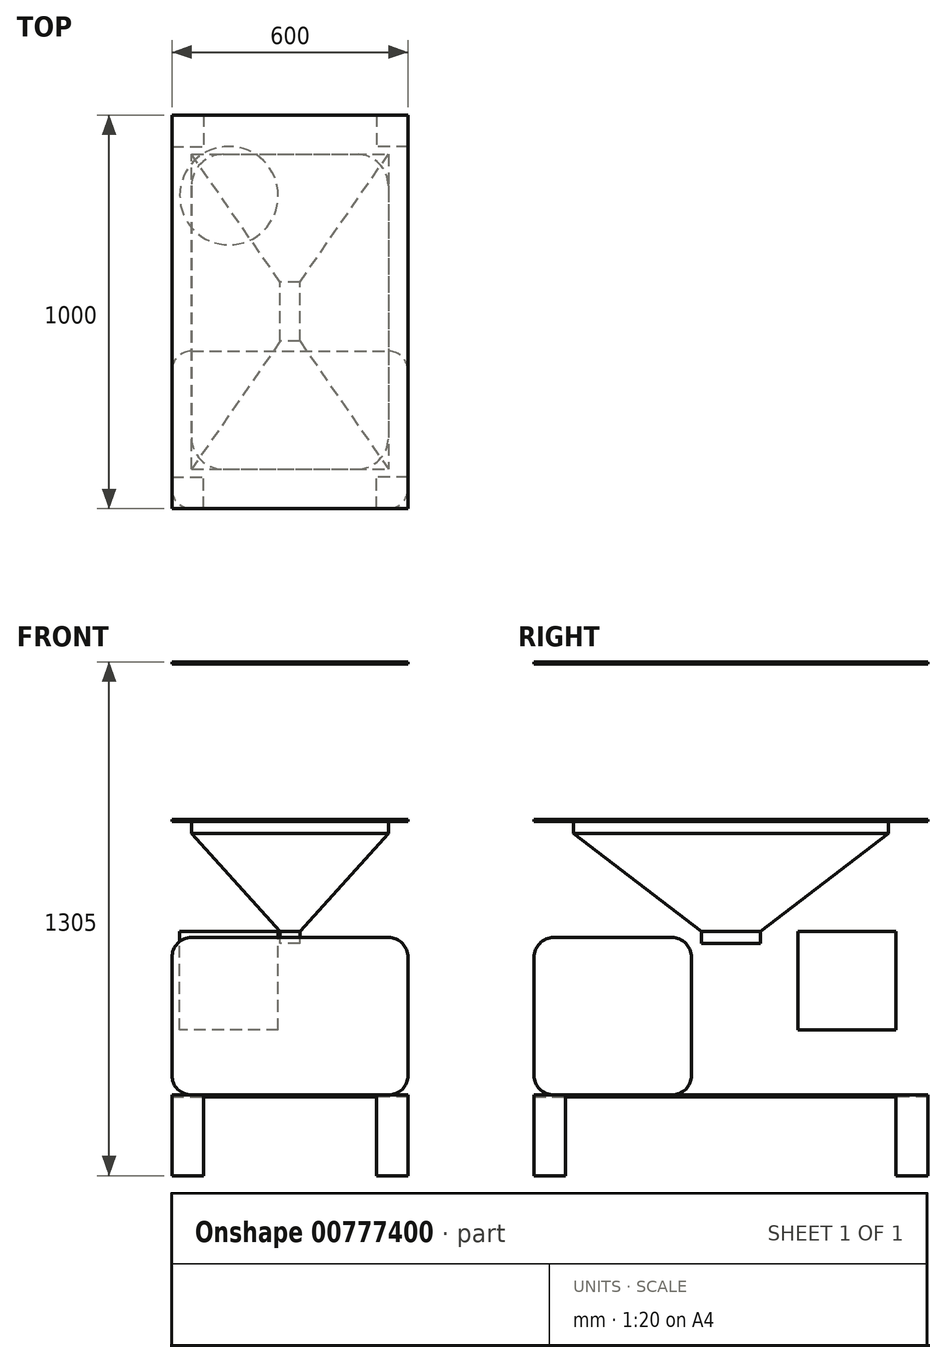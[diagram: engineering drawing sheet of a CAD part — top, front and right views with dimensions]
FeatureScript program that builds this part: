
annotation { "Feature Type Name" : "Feature", "Feature Type Description" : "" }
export const myFeature = defineFeature(function(context is Context, id is Id, definition is map)
    precondition{}
    {
        {
            var Q0;
            Q0=qCreatedBy(makeId("Top.planeOp"),FACE);
            cPlane(context, id + "F0", {"entities" : qUnion([Q0]), "cplaneType" : CPlaneType.OFFSET, "offset" : 450 * mm, "oppositeDirection" : true, "width" : 150 * mm, "height" : 150 * mm});
        }
        {
            var Q0;
            Q0=qCreatedBy(makeId("Top.planeOp"),FACE);
            cPlane(context, id + "F1", {"entities" : qUnion([Q0]), "cplaneType" : CPlaneType.OFFSET, "offset" : 650 * mm, "width" : 150 * mm, "height" : 150 * mm});
        }
        {
            var Q0;
            Q0=qCreatedBy(makeId("Top.planeOp"),FACE);
            cPlane(context, id + "F2", {"entities" : qUnion([Q0]), "cplaneType" : CPlaneType.OFFSET, "offset" : 250 * mm, "width" : 150 * mm, "height" : 150 * mm});
        }
        {
            var Q0;
            Q0=qCreatedBy(makeId("Top.planeOp"),FACE);
            cPlane(context, id + "F3", {"entities" : qUnion([Q0]), "cplaneType" : CPlaneType.OFFSET, "offset" : 30 * mm, "oppositeDirection" : true, "width" : 150 * mm, "height" : 150 * mm});
        }
        {
            var Q0;
            Q0=qCreatedBy(id+"F0.planeOp",FACE);
            var sketch = newSketch(context, id + "F4", { "sketchPlane" : qUnion([Q0])});
            skLineSegment(sketch, "E0.bottom", {"start": v(-300, 500) * mm, "end": v(300, 500) * mm});
            skLineSegment(sketch, "E0.top", {"start": v(-300, -500) * mm, "end": v(300, -500) * mm});
            skLineSegment(sketch, "E0.left", {"start": v(-300, 500) * mm, "end": v(-300, -500) * mm});
            skLineSegment(sketch, "E0.right", {"start": v(300, 500) * mm, "end": v(300, -500) * mm});
            skPoint(sketch, "E0.middle", {"position": v(0, 0) * mm});
            skSolve(sketch);
        }
        {
            var Q0;
            Q0 = qSketchRegion(id + "F4", true);
            extrude(context, id + "F5", {"entities" : qUnion([Q0]), "depth" : 5 * mm, "offsetDistance" : 25 * mm});
        }
        {
            var Q0;
            Q0=makeQuery(id+"F5.opExtrude","CAP_FACE",FACE,{"disambiguationData":[OSD([sQuery(id+"F4.wireOp",EDGE,"E0.bottom"),sQuery(id+"F4.wireOp",EDGE,"E0.top"),sQuery(id+"F4.wireOp",EDGE,"E0.left"),sQuery(id+"F4.wireOp",EDGE,"E0.right")])],"isStart":false});
            var sketch = newSketch(context, id + "F6", { "sketchPlane" : qUnion([Q0])});
            skPoint(sketch, "E1.0.3.start.orphan", {"position": v(300, 500) * mm});
            skPoint(sketch, "E1.0.0.start.orphan", {"position": v(-300, 500) * mm});
            skPoint(sketch, "E1.0.1.end.orphan", {"position": v(300, -500) * mm});
            skPoint(sketch, "E1.0.1.start.orphan", {"position": v(-300, -500) * mm});
            skLineSegment(sketch, "E2.bottom", {"start": v(-250, -500) * mm, "end": v(250, -500) * mm});
            skLineSegment(sketch, "E2.top", {"start": v(-250, -100) * mm, "end": v(250, -100) * mm});
            skLineSegment(sketch, "E2.left", {"start": v(-300, -450) * mm, "end": v(-300, -150) * mm});
            skLineSegment(sketch, "E2.right", {"start": v(300, -450) * mm, "end": v(300, -150) * mm});
            skPoint(sketch, "E3.visualSharp", {"position": v(-300, -100) * mm});
            skArc(sketch, "E3.filletArc", {"start": v(-250, -100) * mm, "mid": v(-285.36, -114.64) * mm, "end": v(-300, -150) * mm});
            skPoint(sketch, "E4.visualSharp", {"position": v(300, -100) * mm});
            skArc(sketch, "E4.filletArc", {"start": v(300, -150) * mm, "mid": v(285.36, -114.64) * mm, "end": v(250, -100) * mm});
            skArc(sketch, "E5.filletArc", {"start": v(250, -500) * mm, "mid": v(285.36, -485.36) * mm, "end": v(300, -450) * mm});
            skArc(sketch, "E6.filletArc", {"start": v(-300, -450) * mm, "mid": v(-285.36, -485.36) * mm, "end": v(-250, -500) * mm});
            skSolve(sketch);
        }
        {
            var Q0;
            Q0 = qSketchRegion(id + "F6", true);
            extrude(context, id + "F7", {"entities" : qUnion([Q0]), "depth" : 400 * mm, "offsetDistance" : 25 * mm});
        }
        {
            var Q0;
            Q0=makeQuery(id+"F7.opExtrude","CAP_EDGE",EDGE,{"disambiguationData":[OSD([sQuery(id+"F6.wireOp",EDGE,"E2.right")])],"isStart":false});
            fillet(context, id + "F8", {"entities" : qUnion([Q0]), "radius" : 50 * mm, "tangentPropagation" : true, "allowEdgeOverflow" : false});
        }
        {
            var Q0;
            Q0=makeQuery(id+"F7.opExtrude","CAP_FACE",FACE,{"disambiguationData":[OSD([sQuery(id+"F6.wireOp",EDGE,"E2.bottom"),sQuery(id+"F6.wireOp",EDGE,"E2.top"),sQuery(id+"F6.wireOp",EDGE,"E2.left"),sQuery(id+"F6.wireOp",EDGE,"E2.right"),sQuery(id+"F6.wireOp",EDGE,"E3.filletArc"),sQuery(id+"F6.wireOp",EDGE,"E4.filletArc"),sQuery(id+"F6.wireOp",EDGE,"E5.filletArc"),sQuery(id+"F6.wireOp",EDGE,"E6.filletArc")])],"isStart":true});
            fillet(context, id + "F9", {"entities" : qUnion([Q0]), "radius" : 50 * mm, "tangentPropagation" : true, "allowEdgeOverflow" : false});
        }
        {
            var Q0;
            Q0=qCreatedBy(id+"F2.planeOp",FACE);
            var sketch = newSketch(context, id + "F10", { "sketchPlane" : qUnion([Q0])});
            skLineSegment(sketch, "E7.0.0", {"start": v(-300, 500) * mm, "end": v(-300, -500) * mm});
            skLineSegment(sketch, "E7.0.1", {"start": v(-300, -500) * mm, "end": v(300, -500) * mm});
            skLineSegment(sketch, "E7.0.2", {"start": v(300, -500) * mm, "end": v(300, 500) * mm});
            skLineSegment(sketch, "E7.0.3", {"start": v(300, 500) * mm, "end": v(-300, 500) * mm});
            skSolve(sketch);
        }
        {
            var Q0;
            Q0 = qSketchRegion(id + "F10", true);
            extrude(context, id + "F11", {"entities" : qUnion([Q0]), "depth" : 5 * mm, "offsetDistance" : 25 * mm});
        }
        {
            var Q0;
            Q0=makeQuery(id+"F11.opExtrude","CAP_FACE",FACE,{"disambiguationData":[OSD([sQuery(id+"F10.wireOp",EDGE,"E7.0.0"),sQuery(id+"F10.wireOp",EDGE,"E7.0.1"),sQuery(id+"F10.wireOp",EDGE,"E7.0.2"),sQuery(id+"F10.wireOp",EDGE,"E7.0.3")])],"isStart":false});
            var sketch = newSketch(context, id + "F12", { "sketchPlane" : qUnion([Q0])});
            skLineSegment(sketch, "E8.bottom", {"start": v(-170, 400) * mm, "end": v(170, 400) * mm});
            skLineSegment(sketch, "E8.top", {"start": v(-170, -400) * mm, "end": v(170, -400) * mm});
            skLineSegment(sketch, "E8.left", {"start": v(-250, 320) * mm, "end": v(-250, -320) * mm});
            skLineSegment(sketch, "E8.right", {"start": v(250, 320) * mm, "end": v(250, -320) * mm});
            skPoint(sketch, "E8.middle", {"position": v(0, 0) * mm});
            skPoint(sketch, "E9.visualSharp", {"position": v(-250, 400) * mm});
            skArc(sketch, "E9.filletArc", {"start": v(-170, 400) * mm, "mid": v(-226.57, 376.57) * mm, "end": v(-250, 320) * mm});
            skPoint(sketch, "E10.visualSharp", {"position": v(250, 400) * mm});
            skArc(sketch, "E10.filletArc", {"start": v(250, 320) * mm, "mid": v(226.57, 376.57) * mm, "end": v(170, 400) * mm});
            skPoint(sketch, "E11.visualSharp", {"position": v(-250, -400) * mm});
            skArc(sketch, "E11.filletArc", {"start": v(-250, -320) * mm, "mid": v(-226.57, -376.57) * mm, "end": v(-170, -400) * mm});
            skPoint(sketch, "E12.visualSharp", {"position": v(250, -400) * mm});
            skArc(sketch, "E12.filletArc", {"start": v(170, -400) * mm, "mid": v(226.57, -376.57) * mm, "end": v(250, -320) * mm});
            skSolve(sketch);
        }
        {
            var Q0;
            Q0 = qSketchRegion(id + "F12", true);
            extrude(context, id + "F13", {"entities" : qUnion([Q0]), "operationType" : NewBodyOperationType.REMOVE, "endBound" : BoundingType.SYMMETRIC, "oppositeDirection" : true, "depth" : 10 * mm, "offsetDistance" : 25 * mm});
        }
        {
            var Q0;
            Q0=makeQuery(id+"F11.opExtrude","CAP_FACE",FACE,{"disambiguationData":[OSD([sQuery(id+"F10.wireOp",EDGE,"E7.0.0"),sQuery(id+"F10.wireOp",EDGE,"E7.0.1"),sQuery(id+"F10.wireOp",EDGE,"E7.0.2"),sQuery(id+"F10.wireOp",EDGE,"E7.0.3")])],"isStart":true});
            var sketch = newSketch(context, id + "F14", { "sketchPlane" : qUnion([Q0])});
            skLineSegment(sketch, "E13.0", {"start": v(-170, 400) * mm, "end": v(170, 400) * mm});
            skLineSegment(sketch, "E14.0", {"start": v(250, -320) * mm, "end": v(250, 320) * mm});
            skLineSegment(sketch, "E15.0", {"start": v(-170, -400) * mm, "end": v(170, -400) * mm});
            skLineSegment(sketch, "E16.0", {"start": v(-250, -320) * mm, "end": v(-250, 320) * mm});
            skLineSegment(sketch, "E17", {"start": v(-250, -320) * mm, "end": v(-250, -400) * mm});
            skLineSegment(sketch, "E18", {"start": v(-250, -400) * mm, "end": v(-170, -400) * mm});
            skLineSegment(sketch, "E19", {"start": v(170, -400) * mm, "end": v(250, -400) * mm});
            skLineSegment(sketch, "E20", {"start": v(250, -400) * mm, "end": v(250, -320) * mm});
            skLineSegment(sketch, "E21", {"start": v(-250, 320) * mm, "end": v(-250, 400) * mm});
            skLineSegment(sketch, "E22", {"start": v(-250, 400) * mm, "end": v(-170, 400) * mm});
            skLineSegment(sketch, "E23", {"start": v(170, 400) * mm, "end": v(250, 400) * mm});
            skLineSegment(sketch, "E24", {"start": v(250, 400) * mm, "end": v(250, 320) * mm});
            skSolve(sketch);
        }
        {
            var Q0;
            Q0 = qSketchRegion(id + "F14", true);
            extrude(context, id + "F15", {"entities" : qUnion([Q0]), "depth" : 30 * mm, "offsetDistance" : 25 * mm});
        }
        {
            var Q0;
            Q0=qCreatedBy(id+"F3.planeOp",FACE);
            var sketch = newSketch(context, id + "F16", { "sketchPlane" : qUnion([Q0])});
            skCircle(sketch, "E25", {"center": v(-155, 295) * mm, "radius": 125 * mm});
            skLineSegment(sketch, "E26.0.0", {"start": v(300, -500) * mm, "end": v(300, 500) * mm, "construction": true});
            skLineSegment(sketch, "E26.0.1", {"start": v(300, 500) * mm, "end": v(-300, 500) * mm, "construction": true});
            skLineSegment(sketch, "E26.0.2", {"start": v(-300, 500) * mm, "end": v(-300, -500) * mm, "construction": true});
            skLineSegment(sketch, "E26.0.3", {"start": v(-300, -500) * mm, "end": v(300, -500) * mm, "construction": true});
            skSolve(sketch);
        }
        {
            var Q0;
            Q0 = qSketchRegion(id + "F16", true);
            extrude(context, id + "F17", {"entities" : qUnion([Q0]), "oppositeDirection" : true, "depth" : 250 * mm, "offsetDistance" : 25 * mm});
        }
        {
            var Q0;
            Q0=qCreatedBy(id+"F3.planeOp",FACE);
            var sketch = newSketch(context, id + "F18", { "sketchPlane" : qUnion([Q0])});
            skLineSegment(sketch, "E27.bottom", {"start": v(25, -75) * mm, "end": v(-25, -75) * mm});
            skLineSegment(sketch, "E27.top", {"start": v(25, 75) * mm, "end": v(-25, 75) * mm});
            skLineSegment(sketch, "E27.left", {"start": v(25, -75) * mm, "end": v(25, 75) * mm});
            skLineSegment(sketch, "E27.right", {"start": v(-25, -75) * mm, "end": v(-25, 75) * mm});
            skPoint(sketch, "E27.middle", {"position": v(0, 0) * mm});
            skSolve(sketch);
        }
        {
            var Q0;
            Q0 = qSketchRegion(id + "F18", true);
            extrude(context, id + "F19", {"entities" : qUnion([Q0]), "oppositeDirection" : true, "depth" : 30 * mm, "offsetDistance" : 25 * mm});
        }
        {
            var Q0;
            Q0=makeQuery(id+"F19.opExtrude","CAP_FACE",FACE,{"disambiguationData":[OSD([sQuery(id+"F18.wireOp",EDGE,"E27.bottom"),sQuery(id+"F18.wireOp",EDGE,"E27.top"),sQuery(id+"F18.wireOp",EDGE,"E27.left"),sQuery(id+"F18.wireOp",EDGE,"E27.right")])],"isStart":true});
            var Q1;
            Q1=makeQuery(id+"F15.opExtrude","CAP_FACE",FACE,{"disambiguationData":[OSD([sQuery(id+"F14.wireOp",EDGE,"E13.0"),sQuery(id+"F14.wireOp",EDGE,"E14.0"),sQuery(id+"F14.wireOp",EDGE,"E15.0"),sQuery(id+"F14.wireOp",EDGE,"E16.0"),sQuery(id+"F14.wireOp",EDGE,"E17"),sQuery(id+"F14.wireOp",EDGE,"E18"),sQuery(id+"F14.wireOp",EDGE,"E19"),sQuery(id+"F14.wireOp",EDGE,"E20"),sQuery(id+"F14.wireOp",EDGE,"E21"),sQuery(id+"F14.wireOp",EDGE,"E22"),sQuery(id+"F14.wireOp",EDGE,"E23"),sQuery(id+"F14.wireOp",EDGE,"E24")])],"isStart":false});
            loft(context, id + "F20", {"operationType" : NewBodyOperationType.ADD, "sheetProfilesArray" : [{ "sheetProfileEntities" : qUnion([Q0]) }, { "sheetProfileEntities" : qUnion([Q1]) }]});
        }
        {
            var Q0;
            Q0=qCreatedBy(id+"F1.planeOp",FACE);
            var sketch = newSketch(context, id + "F21", { "sketchPlane" : qUnion([Q0])});
            skLineSegment(sketch, "E28.0.0", {"start": v(300, -500) * mm, "end": v(300, 500) * mm});
            skLineSegment(sketch, "E28.0.1", {"start": v(300, 500) * mm, "end": v(-300, 500) * mm});
            skLineSegment(sketch, "E28.0.2", {"start": v(-300, 500) * mm, "end": v(-300, -500) * mm});
            skLineSegment(sketch, "E28.0.3", {"start": v(-300, -500) * mm, "end": v(300, -500) * mm});
            skSolve(sketch);
        }
        {
            var Q0;
            Q0 = qSketchRegion(id + "F21", true);
            extrude(context, id + "F22", {"entities" : qUnion([Q0]), "depth" : 5 * mm, "offsetDistance" : 25 * mm});
        }
        {
            var Q0;
            Q0=makeQuery(id+"F5.opExtrude","CAP_FACE",FACE,{"disambiguationData":[OSD([sQuery(id+"F4.wireOp",EDGE,"E0.bottom"),sQuery(id+"F4.wireOp",EDGE,"E0.top"),sQuery(id+"F4.wireOp",EDGE,"E0.left"),sQuery(id+"F4.wireOp",EDGE,"E0.right")])],"isStart":true});
            var sketch = newSketch(context, id + "F23", { "sketchPlane" : qUnion([Q0])});
            skLineSegment(sketch, "E29.0.1", {"start": v(-300, -500) * mm, "end": v(300, -500) * mm, "construction": true});
            skLineSegment(sketch, "E30.bottom", {"start": v(-300, 500) * mm, "end": v(-220, 500) * mm});
            skLineSegment(sketch, "E30.top", {"start": v(-300, 420) * mm, "end": v(-220, 420) * mm});
            skLineSegment(sketch, "E30.left", {"start": v(-300, 500) * mm, "end": v(-300, 420) * mm});
            skLineSegment(sketch, "E30.right", {"start": v(-220, 500) * mm, "end": v(-220, 420) * mm});
            skLineSegment(sketch, "E31.bottom", {"start": v(300, 500) * mm, "end": v(220, 500) * mm});
            skLineSegment(sketch, "E31.top", {"start": v(300, 420) * mm, "end": v(220, 420) * mm});
            skLineSegment(sketch, "E31.left", {"start": v(300, 500) * mm, "end": v(300, 420) * mm});
            skLineSegment(sketch, "E31.right", {"start": v(220, 500) * mm, "end": v(220, 420) * mm});
            skLineSegment(sketch, "E32", {"start": v(-117.18, 0) * mm, "end": v(133.05, 0) * mm, "construction": true});
            skLineSegment(sketch, "E33.MirrorCS", {"start": v(300, -500) * mm, "end": v(220, -500) * mm});
            skLineSegment(sketch, "E34.MirrorCS", {"start": v(-300, -500) * mm, "end": v(-300, -420) * mm});
            skLineSegment(sketch, "E35.MirrorCS", {"start": v(-220, -500) * mm, "end": v(-220, -420) * mm});
            skLineSegment(sketch, "E36.MirrorCS", {"start": v(220, -500) * mm, "end": v(220, -420) * mm});
            skLineSegment(sketch, "E37.MirrorCS", {"start": v(300, -500) * mm, "end": v(300, -420) * mm});
            skLineSegment(sketch, "E38.MirrorCS", {"start": v(-300, -420) * mm, "end": v(-220, -420) * mm});
            skLineSegment(sketch, "E39.MirrorCS", {"start": v(-300, -500) * mm, "end": v(-220, -500) * mm});
            skLineSegment(sketch, "E40.MirrorCS", {"start": v(300, -420) * mm, "end": v(220, -420) * mm});
            skSolve(sketch);
        }
        {
            var Q0;
            Q0 = qSketchRegion(id + "F23", true);
            extrude(context, id + "F24", {"entities" : qUnion([Q0]), "operationType" : NewBodyOperationType.ADD, "depth" : 200 * mm, "offsetDistance" : 25 * mm});
        }
    });
